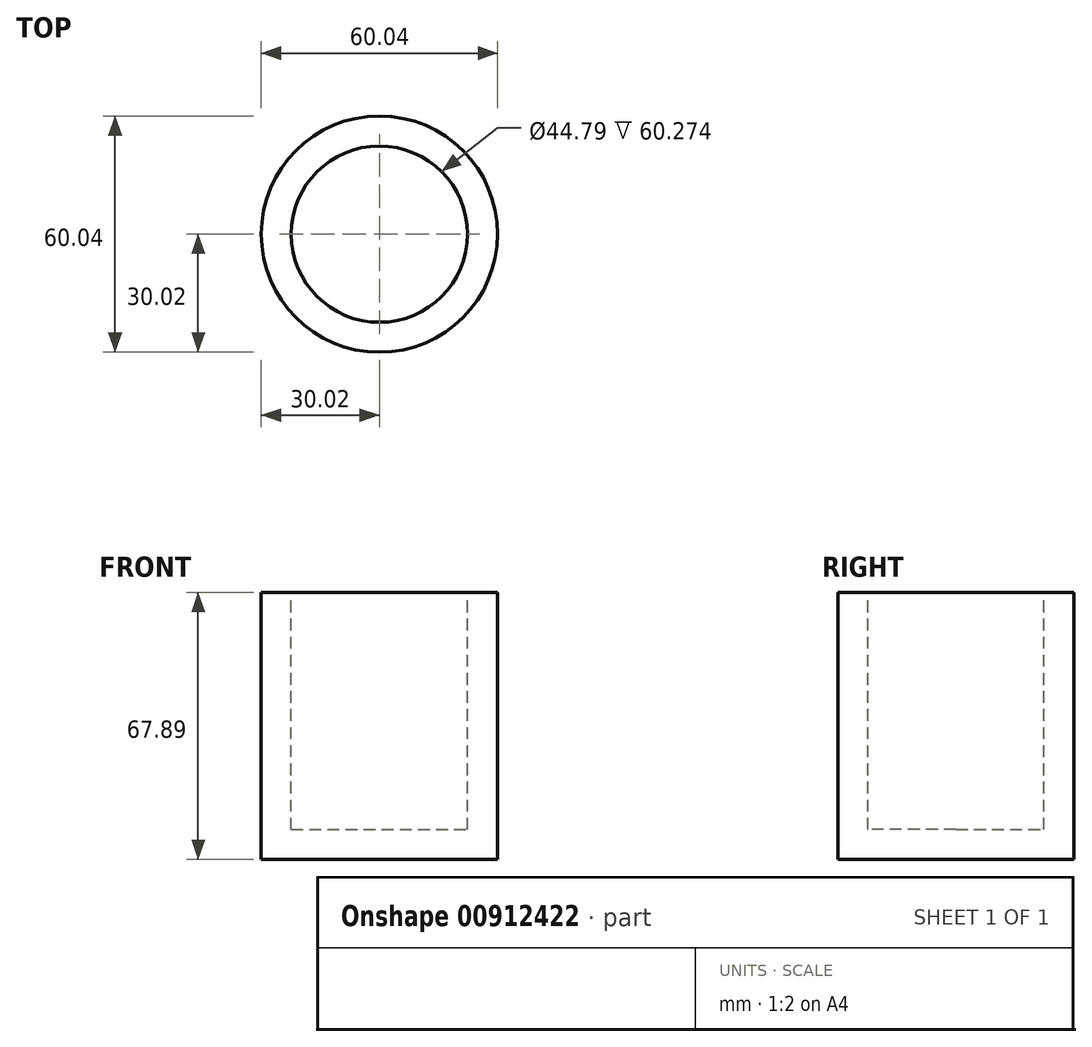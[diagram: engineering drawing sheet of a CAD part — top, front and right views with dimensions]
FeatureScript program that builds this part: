
annotation { "Feature Type Name" : "Feature", "Feature Type Description" : "" }
export const myFeature = defineFeature(function(context is Context, id is Id, definition is map)
    precondition{}
    {
        {
            var Q0;
            Q0=qCreatedBy(makeId("Front.planeOp"),FACE);
            var sketch = newSketch(context, id + "F0", { "sketchPlane" : qUnion([Q0])});
            skLineSegment(sketch, "E0", {"start": v(0, 42.57) * mm, "end": v(0, -57.42) * mm, "construction": true});
            skLineSegment(sketch, "E1", {"start": v(0, 32.3) * mm, "end": v(30.02, 32.3) * mm});
            skLineSegment(sketch, "E2", {"start": v(30.02, 32.3) * mm, "end": v(30.02, -35.58) * mm});
            skLineSegment(sketch, "E3", {"start": v(30.02, -35.58) * mm, "end": v(0, -35.58) * mm});
            skLineSegment(sketch, "E4", {"start": v(0, -35.58) * mm, "end": v(0, 32.3) * mm});
            skSolve(sketch);
        }
        {
            var Q0;
            Q0=makeQuery(id+"F0.imprint","IMPRINT",FACE,{"disambiguationData":[TD([[makeQuery(id+"F0.imprint","IMPRINT",EDGE,{"derivedFrom":sQuery(id+"F0.wireOp",EDGE,"E1")}),-1.0]])]});
            var Q1;
            Q1=sQuery(id+"F0.wireOp",EDGE,"E0");
            revolve(context, id + "F1", {"surfaceOperationType" : NewSurfaceOperationType.NEW, "entities" : qUnion([Q0]), "axis" : qUnion([Q1]), "revolveType" : RevolveType.FULL});
        }
        {
            var Q0;
            Q0=makeQuery(id+"F1.opRevolve","SWEPT_FACE",FACE,{"disambiguationData":[OSD([sQuery(id+"F0.wireOp",EDGE,"E1")])]});
            shell(context, id + "F2", {"entities" : qUnion([Q0]), "thickness" : 7.62 * mm});
        }
        {
            var Q0;
            Q0=qCreatedBy(makeId("Right.planeOp"),FACE);
            var sketch = newSketch(context, id + "F3", { "sketchPlane" : qUnion([Q0])});
            skFitSpline(sketch, "E5", {"points": [v(-27.53, 20.85) * mm, v(-49.77, 0) * mm, v(-28.55, -23.6) * mm], "startDerivative": vector(-86.74, -40.72) * mm, "endDerivative": vector(84.36, -48.15) * mm});
            skSolve(sketch);
        }
        {
            var Q0;
            Q0=sQuery(id+"F3.wireOp",VERTEX,"E5.start");
            var Q1;
            Q1=sQuery(id+"F3.wireOp",EDGE,"E5");
            cPlane(context, id + "F4", {"entities" : qUnion([Q0, Q1]), "cplaneType" : CPlaneType.CURVE_POINT, "offset" : 25.4 * mm, "width" : 152.4 * mm, "height" : 152.4 * mm});
        }
        {
            var Q0;
            Q0=qCreatedBy(id+"F4.planeOp",FACE);
            var sketch = newSketch(context, id + "F5", { "sketchPlane" : qUnion([Q0])});
            skCircle(sketch, "E6", {"center": v(0, 30.57) * mm, "radius": 3.27 * mm});
            skSolve(sketch);
        }
    });
